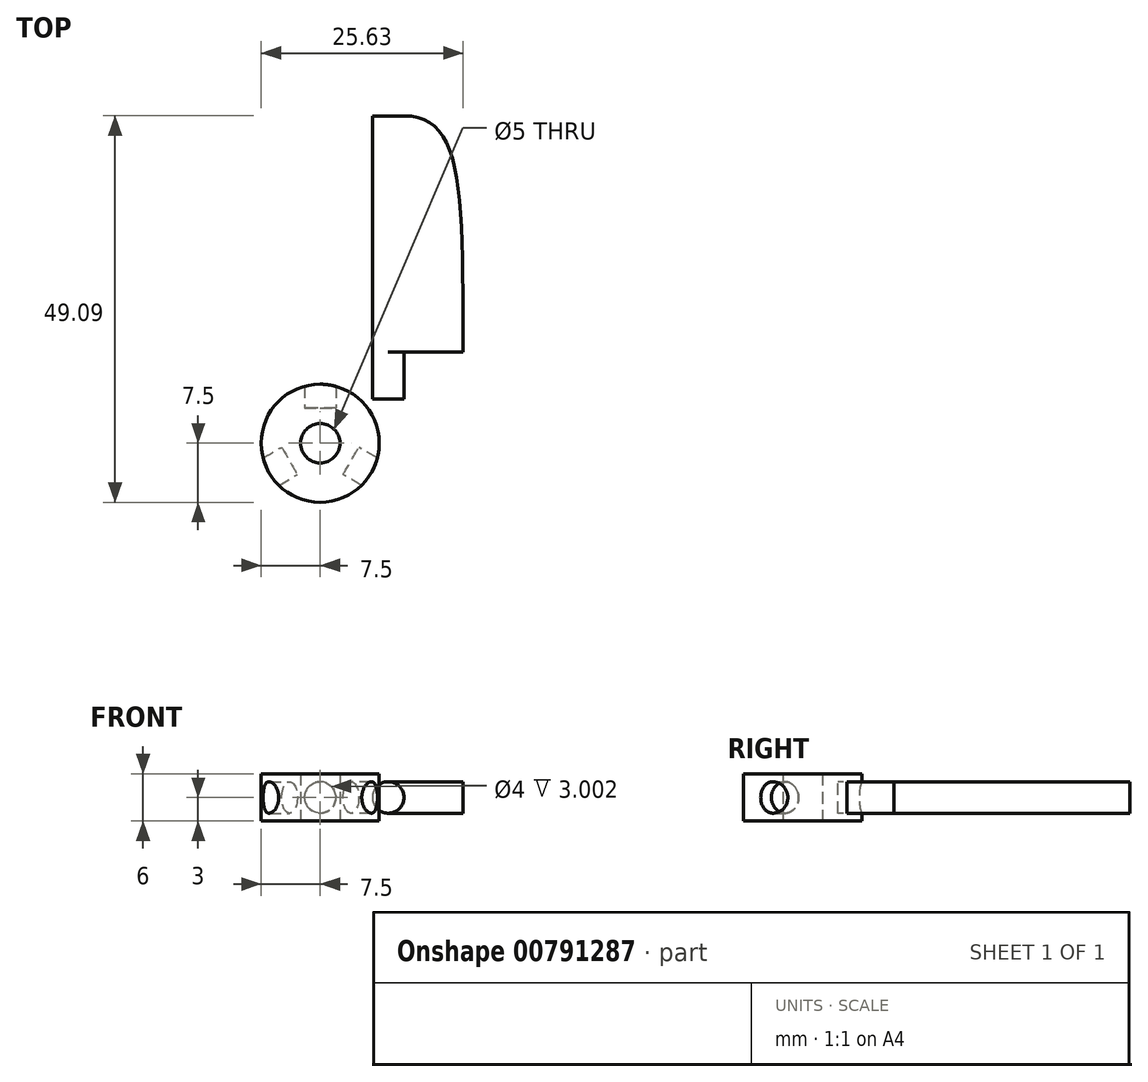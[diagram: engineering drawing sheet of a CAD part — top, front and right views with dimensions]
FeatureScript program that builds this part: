
annotation { "Feature Type Name" : "Feature", "Feature Type Description" : "" }
export const myFeature = defineFeature(function(context is Context, id is Id, definition is map)
    precondition{}
    {
        {
            var Q0;
            Q0=qCreatedBy(makeId("Top.planeOp"),FACE);
            var sketch = newSketch(context, id + "F0", { "sketchPlane" : qUnion([Q0])});
            skCircle(sketch, "E0", {"center": v(0, 0) * mm, "radius": 7.5 * mm});
            skLineSegment(sketch, "E1", {"start": v(10.63, 11.59) * mm, "end": v(18.13, 11.59) * mm});
            skFitSpline(sketch, "E2", {"points": [v(18.13, 11.59) * mm, v(10.63, 41.59) * mm], "startDerivative": vector(0, 62.53) * mm, "endDerivative": vector(-22.5, -0.05) * mm});
            skCircle(sketch, "E3", {"center": v(0, 0) * mm, "radius": 2.5 * mm});
            skLineSegment(sketch, "E4", {"start": v(0, 7.5) * mm, "end": v(0, 4.5) * mm});
            skLineSegment(sketch, "E5", {"start": v(6.5, -3.74) * mm, "end": v(3.9, -2.25) * mm});
            skLineSegment(sketch, "E6", {"start": v(-6.5, -3.75) * mm, "end": v(-3.9, -2.25) * mm});
            skLineSegment(sketch, "E7", {"start": v(3.9, -2.25) * mm, "end": v(4.9, -0.51) * mm});
            skLineSegment(sketch, "E8", {"start": v(-3.9, -2.25) * mm, "end": v(-2.9, -3.98) * mm});
            skLineSegment(sketch, "E9", {"start": v(0, 4.5) * mm, "end": v(-2, 4.5) * mm});
            skLineSegment(sketch, "E10", {"start": v(6.5, -3.74) * mm, "end": v(7.5, -2) * mm});
            skLineSegment(sketch, "E11", {"start": v(4.9, -0.51) * mm, "end": v(7.5, -2) * mm});
            skLineSegment(sketch, "E12", {"start": v(-6.5, -3.75) * mm, "end": v(-5.5, -5.48) * mm});
            skLineSegment(sketch, "E13", {"start": v(-5.5, -5.48) * mm, "end": v(-2.9, -3.98) * mm});
            skLineSegment(sketch, "E14", {"start": v(0, 7.5) * mm, "end": v(-2, 7.5) * mm});
            skLineSegment(sketch, "E15", {"start": v(-2, 7.5) * mm, "end": v(-2, 4.5) * mm});
            skLineSegment(sketch, "E16", {"start": v(10.63, 11.59) * mm, "end": v(8.63, 11.59) * mm});
            skLineSegment(sketch, "E17.bottom", {"start": v(10.63, 41.59) * mm, "end": v(8.63, 41.59) * mm});
            skLineSegment(sketch, "E17.top", {"start": v(10.63, 5.59) * mm, "end": v(8.63, 5.59) * mm});
            skLineSegment(sketch, "E17.left", {"start": v(10.63, 41.59) * mm, "end": v(10.63, 5.59) * mm});
            skLineSegment(sketch, "E17.right", {"start": v(8.63, 41.59) * mm, "end": v(8.63, 5.59) * mm});
            skSolve(sketch);
        }
        {
            var Q0;
            Q0=makeQuery(id+"F0.imprint","IMPRINT",FACE,{"disambiguationData":[TD([[makeQuery(id+"F0.imprint","IMPRINT",EDGE,{"derivedFrom":sQuery(id+"F0.wireOp",EDGE,"E3")}),-1.0]])]});
            var Q1;
            {var subQ5=sQuery(id+"F0.wireOp",EDGE,"E7");Q1=makeQuery(id+"F0.imprint","IMPRINT",FACE,{"disambiguationData":[TD([[makeQuery(id+"F0.imprint","IMPRINT",EDGE,{"derivedFrom":subQ5}),-1.0]])]});}
            var Q2;
            {var subQ0=sQuery(id+"F0.wireOp",EDGE,"JAF7Ja2K-QW9s-dXYT-bgaN-EXwzVaiHsFTH");var subQ3=sQuery(id+"F0.wireOp",EDGE,"E4");var subQ5=makeQuery(id+"F0.imprint","INTERSECT",VERTEX,{"derivedFrom":[subQ0,subQ3]});Q2=makeQuery(id+"F0.imprint","IMPRINT",FACE,{"disambiguationData":[TD([[makeQuery(id+"F0.imprint","IMPRINT",EDGE,{"disambiguationData":[TD([[subQ5,-1.0]])],"derivedFrom":subQ0}),1.0]])]});}
            var Q3;
            {var subQ0=sQuery(id+"F0.wireOp",EDGE,"JAF7Ja2K-QW9s-dXYT-bgaN-EXwzVaiHsFTH");var subQ3=sQuery(id+"F0.wireOp",EDGE,"E4");var subQ5=makeQuery(id+"F0.imprint","INTERSECT",VERTEX,{"derivedFrom":[subQ0,subQ3]});Q3=makeQuery(id+"F0.imprint","IMPRINT",FACE,{"disambiguationData":[TD([[makeQuery(id+"F0.imprint","IMPRINT",EDGE,{"disambiguationData":[TD([[subQ5,1.0]])],"derivedFrom":subQ0}),1.0]])]});}
            var Q4;
            {var subQ0=sQuery(id+"F0.wireOp",EDGE,"E5");var subQ3=sQuery(id+"F0.wireOp",EDGE,"ulGnR4qZ-HgEX-c6pI-kPwP-CD4F2GIFb5FO");var subQ5=makeQuery(id+"F0.imprint","INTERSECT",VERTEX,{"derivedFrom":[subQ3,subQ0]});Q4=makeQuery(id+"F0.imprint","IMPRINT",FACE,{"disambiguationData":[TD([[makeQuery(id+"F0.imprint","IMPRINT",EDGE,{"disambiguationData":[TD([[subQ5,1.0]])],"derivedFrom":subQ3}),1.0]])]});}
            var Q5;
            {var subQ0=sQuery(id+"F0.wireOp",EDGE,"ulGnR4qZ-HgEX-c6pI-kPwP-CD4F2GIFb5FO");var subQ3=sQuery(id+"F0.wireOp",EDGE,"E5");var subQ5=makeQuery(id+"F0.imprint","INTERSECT",VERTEX,{"derivedFrom":[subQ0,subQ3]});Q5=makeQuery(id+"F0.imprint","IMPRINT",FACE,{"disambiguationData":[TD([[makeQuery(id+"F0.imprint","IMPRINT",EDGE,{"disambiguationData":[TD([[subQ5,-1.0]])],"derivedFrom":subQ0}),1.0]])]});}
            var Q6;
            {var subQ0=sQuery(id+"F0.wireOp",EDGE,"TyoQLf8A-3JJz-OInP-mZb6-aYUDhpHZr2cR");var subQ3=sQuery(id+"F0.wireOp",EDGE,"E6");var subQ5=makeQuery(id+"F0.imprint","INTERSECT",VERTEX,{"derivedFrom":[subQ0,subQ3]});Q6=makeQuery(id+"F0.imprint","IMPRINT",FACE,{"disambiguationData":[TD([[makeQuery(id+"F0.imprint","IMPRINT",EDGE,{"disambiguationData":[TD([[subQ5,-1.0]])],"derivedFrom":subQ0}),1.0]])]});}
            var Q7;
            {var subQ0=sQuery(id+"F0.wireOp",EDGE,"TyoQLf8A-3JJz-OInP-mZb6-aYUDhpHZr2cR");var subQ3=sQuery(id+"F0.wireOp",EDGE,"E6");var subQ5=makeQuery(id+"F0.imprint","INTERSECT",VERTEX,{"derivedFrom":[subQ0,subQ3]});Q7=makeQuery(id+"F0.imprint","IMPRINT",FACE,{"disambiguationData":[TD([[makeQuery(id+"F0.imprint","IMPRINT",EDGE,{"disambiguationData":[TD([[subQ5,1.0]])],"derivedFrom":subQ0}),1.0]])]});}
            var Q8;
            {var subQ4=sQuery(id+"F0.wireOp",EDGE,"E9");Q8=makeQuery(id+"F0.imprint","IMPRINT",FACE,{"disambiguationData":[TD([[makeQuery(id+"F0.imprint","IMPRINT",EDGE,{"derivedFrom":subQ4}),-1.0]])]});}
            var Q9;
            {var subQ4=sQuery(id+"F0.wireOp",EDGE,"E8");Q9=makeQuery(id+"F0.imprint","IMPRINT",FACE,{"disambiguationData":[TD([[makeQuery(id+"F0.imprint","IMPRINT",EDGE,{"derivedFrom":subQ4}),-1.0]])]});}
            extrude(context, id + "F1", {"entities" : qUnion([Q0, Q1, Q2, Q3, Q4, Q5, Q6, Q7, Q8, Q9]), "endBound" : BoundingType.SYMMETRIC, "depth" : 6 * mm, "offsetDistance" : 25 * mm});
        }
        {
            var Q0;
            {var subQ0=sQuery(id+"F0.wireOp",EDGE,"E16");Q0=makeQuery(id+"F0.imprint","IMPRINT",FACE,{"disambiguationData":[TD([[makeQuery(id+"F0.imprint","IMPRINT",EDGE,{"derivedFrom":subQ0}),-1.0]])]});}
            var Q1;
            {var subQ0=sQuery(id+"F0.wireOp",EDGE,"E16");Q1=makeQuery(id+"F0.imprint","IMPRINT",FACE,{"disambiguationData":[TD([[makeQuery(id+"F0.imprint","IMPRINT",EDGE,{"derivedFrom":subQ0}),1.0]])]});}
            var Q2;
            Q2=sQuery(id+"F0.wireOp",EDGE,"E17.right");
            revolve(context, id + "F2", {"surfaceOperationType" : NewSurfaceOperationType.NEW, "entities" : qUnion([Q0, Q1]), "axis" : qUnion([Q2]), "revolveType" : RevolveType.FULL});
        }
        {
            var Q0;
            {var subQ3=sQuery(id+"F0.wireOp",EDGE,"E16");Q0=makeQuery(id+"F0.imprint","IMPRINT",FACE,{"disambiguationData":[TD([[makeQuery(id+"F0.imprint","IMPRINT",EDGE,{"derivedFrom":subQ3}),-1.0]])]});}
            var Q1;
            {var subQ2=sQuery(id+"F0.wireOp",EDGE,"E1");Q1=makeQuery(id+"F0.imprint","IMPRINT",FACE,{"disambiguationData":[TD([[makeQuery(id+"F0.imprint","IMPRINT",EDGE,{"derivedFrom":subQ2}),1.0]])]});}
            extrude(context, id + "F3", {"entities" : qUnion([Q0, Q1]), "operationType" : NewBodyOperationType.ADD, "endBound" : BoundingType.SYMMETRIC, "depth" : 4 * mm, "offsetDistance" : 25 * mm});
        }
        {
            var Q0;
            {var subQ0=sQuery(id+"F0.wireOp",EDGE,"E5");Q0=makeQuery(id+"F0.imprint","IMPRINT",FACE,{"disambiguationData":[TD([[makeQuery(id+"F0.imprint","IMPRINT",EDGE,{"derivedFrom":subQ0}),-1.0]])]});}
            var Q1;
            {var subQ0=sQuery(id+"F0.wireOp",EDGE,"E10");Q1=makeQuery(id+"F0.imprint","IMPRINT",FACE,{"disambiguationData":[TD([[makeQuery(id+"F0.imprint","IMPRINT",EDGE,{"derivedFrom":subQ0}),1.0]])]});}
            var Q2;
            Q2=sQuery(id+"F0.wireOp",EDGE,"E5");
            revolve(context, id + "F4", {"operationType" : NewBodyOperationType.REMOVE, "surfaceOperationType" : NewSurfaceOperationType.NEW, "entities" : qUnion([Q0, Q1]), "axis" : qUnion([Q2]), "revolveType" : RevolveType.FULL, "oppositeDirection" : true});
        }
        {
            var Q0;
            {var subQ0=sQuery(id+"F0.wireOp",EDGE,"E4");Q0=makeQuery(id+"F0.imprint","IMPRINT",FACE,{"disambiguationData":[TD([[makeQuery(id+"F0.imprint","IMPRINT",EDGE,{"derivedFrom":subQ0}),-1.0]])]});}
            var Q1;
            {var subQ0=sQuery(id+"F0.wireOp",EDGE,"E14");Q1=makeQuery(id+"F0.imprint","IMPRINT",FACE,{"disambiguationData":[TD([[makeQuery(id+"F0.imprint","IMPRINT",EDGE,{"derivedFrom":subQ0}),1.0]])]});}
            var Q2;
            Q2=sQuery(id+"F0.wireOp",EDGE,"E4");
            revolve(context, id + "F5", {"operationType" : NewBodyOperationType.REMOVE, "surfaceOperationType" : NewSurfaceOperationType.NEW, "entities" : qUnion([Q0, Q1]), "axis" : qUnion([Q2]), "revolveType" : RevolveType.FULL, "oppositeDirection" : true});
        }
        {
            var Q0;
            {var subQ0=sQuery(id+"F0.wireOp",EDGE,"E6");Q0=makeQuery(id+"F0.imprint","IMPRINT",FACE,{"disambiguationData":[TD([[makeQuery(id+"F0.imprint","IMPRINT",EDGE,{"derivedFrom":subQ0}),-1.0]])]});}
            var Q1;
            {var subQ0=sQuery(id+"F0.wireOp",EDGE,"E12");Q1=makeQuery(id+"F0.imprint","IMPRINT",FACE,{"disambiguationData":[TD([[makeQuery(id+"F0.imprint","IMPRINT",EDGE,{"derivedFrom":subQ0}),1.0]])]});}
            var Q2;
            Q2=sQuery(id+"F0.wireOp",EDGE,"E6");
            revolve(context, id + "F6", {"operationType" : NewBodyOperationType.REMOVE, "surfaceOperationType" : NewSurfaceOperationType.NEW, "entities" : qUnion([Q0, Q1]), "axis" : qUnion([Q2]), "revolveType" : RevolveType.FULL, "oppositeDirection" : true});
        }
    });
